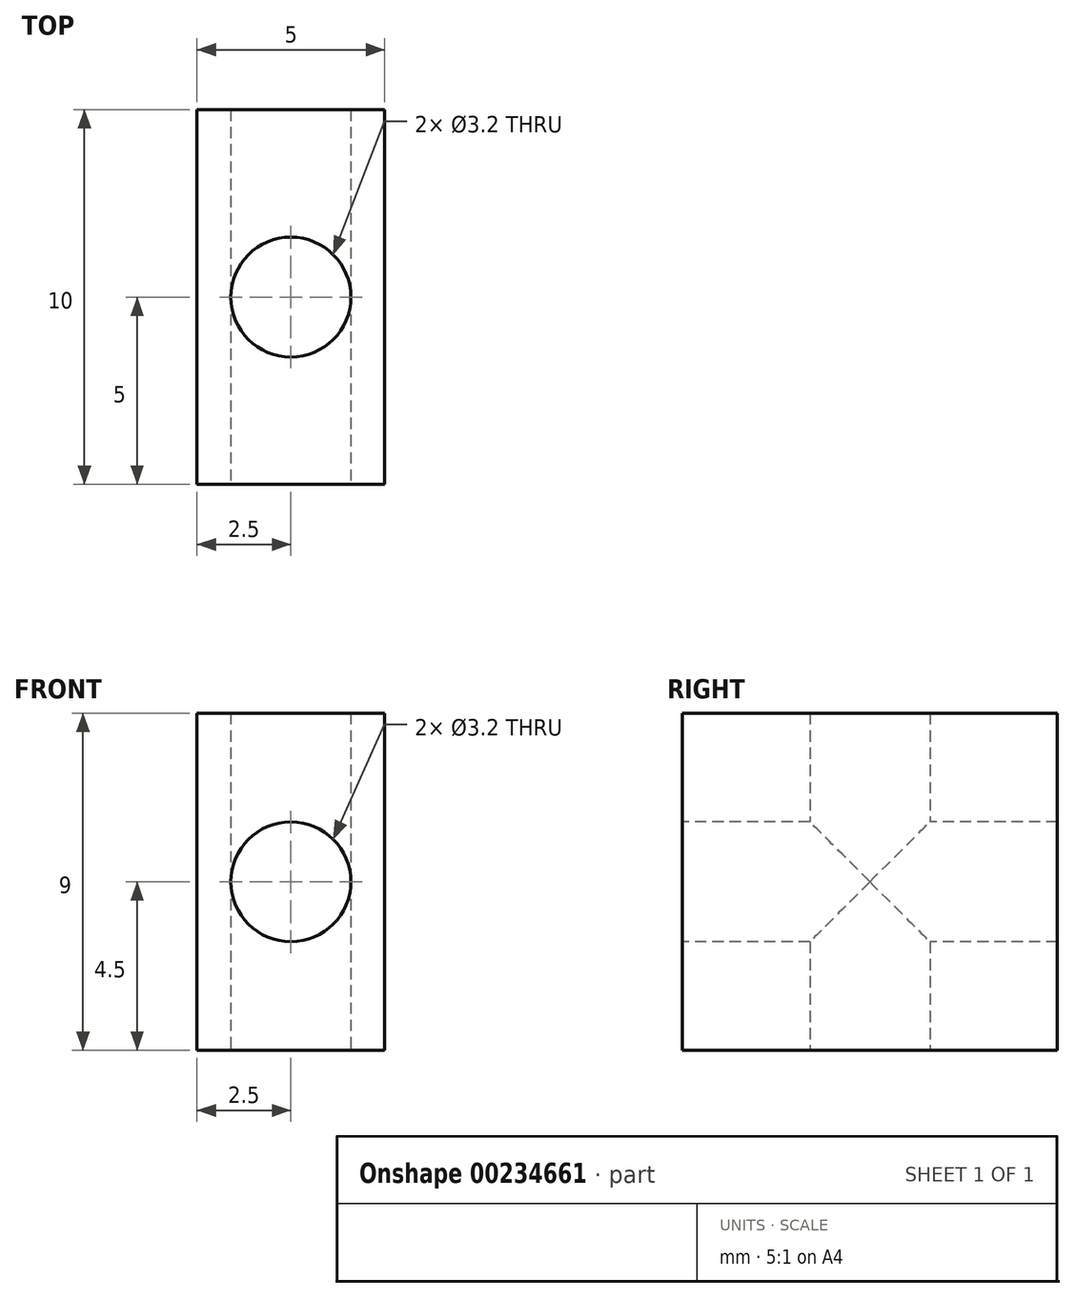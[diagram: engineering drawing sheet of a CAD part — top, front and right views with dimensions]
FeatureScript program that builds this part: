
annotation { "Feature Type Name" : "Feature", "Feature Type Description" : "" }
export const myFeature = defineFeature(function(context is Context, id is Id, definition is map)
    precondition{}
    {
        {
            var Q0;
            Q0=qCreatedBy(makeId("Top.planeOp"),FACE);
            var sketch = newSketch(context, id + "F0", { "sketchPlane" : qUnion([Q0])});
            skLineSegment(sketch, "E0.bottom", {"start": v(2.5, 5) * mm, "end": v(-2.5, 5) * mm});
            skLineSegment(sketch, "E0.top", {"start": v(2.5, -5) * mm, "end": v(-2.5, -5) * mm});
            skLineSegment(sketch, "E0.left", {"start": v(2.5, 5) * mm, "end": v(2.5, -5) * mm});
            skLineSegment(sketch, "E0.right", {"start": v(-2.5, 5) * mm, "end": v(-2.5, -5) * mm});
            skPoint(sketch, "E0.middle", {"position": v(0, 0) * mm});
            skCircle(sketch, "E1", {"center": v(0, 0) * mm, "radius": 1.6 * mm});
            skSolve(sketch);
        }
        {
            var Q0;
            Q0=makeQuery(id+"F0.imprint","IMPRINT",FACE,{"disambiguationData":[TD([[makeQuery(id+"F0.imprint","IMPRINT",EDGE,{"derivedFrom":sQuery(id+"F0.wireOp",EDGE,"E0.bottom")}),1.0]])]});
            extrude(context, id + "F1", {"entities" : qUnion([Q0]), "depth" : 9 * mm});
        }
        {
            var Q0;
            Q0=makeQuery(id+"F1.opExtrude","SWEPT_FACE",FACE,{"disambiguationData":[OSD([sQuery(id+"F0.wireOp",EDGE,"E0.top")])]});
            var sketch = newSketch(context, id + "F2", { "sketchPlane" : qUnion([Q0])});
            skLineSegment(sketch, "E2", {"start": v(0, 9) * mm, "end": v(0, 0) * mm});
            skCircle(sketch, "E3", {"center": v(0, 4.5) * mm, "radius": 1.6 * mm});
            skSolve(sketch);
        }
        {
            var Q0;
            {var subQ0=sQuery(id+"F2.wireOp",EDGE,"E3");var subQ1=sQuery(id+"F2.wireOp",EDGE,"E2");var subQ2=makeQuery(id+"F2.imprint","INTERSECT",VERTEX,{"disambiguationData":[OD(0.0)],"derivedFrom":[subQ1,subQ0]});Q0=makeQuery(id+"F2.imprint","IMPRINT",FACE,{"disambiguationData":[TD([[makeQuery(id+"F2.imprint","IMPRINT",EDGE,{"disambiguationData":[TD([[subQ2,-1.0]])],"derivedFrom":subQ1}),-1.0]])]});}
            var Q1;
            {var subQ0=sQuery(id+"F2.wireOp",EDGE,"E3");var subQ1=sQuery(id+"F2.wireOp",EDGE,"E2");var subQ2=makeQuery(id+"F2.imprint","INTERSECT",VERTEX,{"disambiguationData":[OD(0.0)],"derivedFrom":[subQ1,subQ0]});Q1=makeQuery(id+"F2.imprint","IMPRINT",FACE,{"disambiguationData":[TD([[makeQuery(id+"F2.imprint","IMPRINT",EDGE,{"disambiguationData":[TD([[subQ2,-1.0]])],"derivedFrom":subQ1}),1.0]])]});}
            extrude(context, id + "F3", {"entities" : qUnion([Q0, Q1]), "operationType" : NewBodyOperationType.REMOVE, "oppositeDirection" : true, "depth" : 25 * mm});
        }
    });
